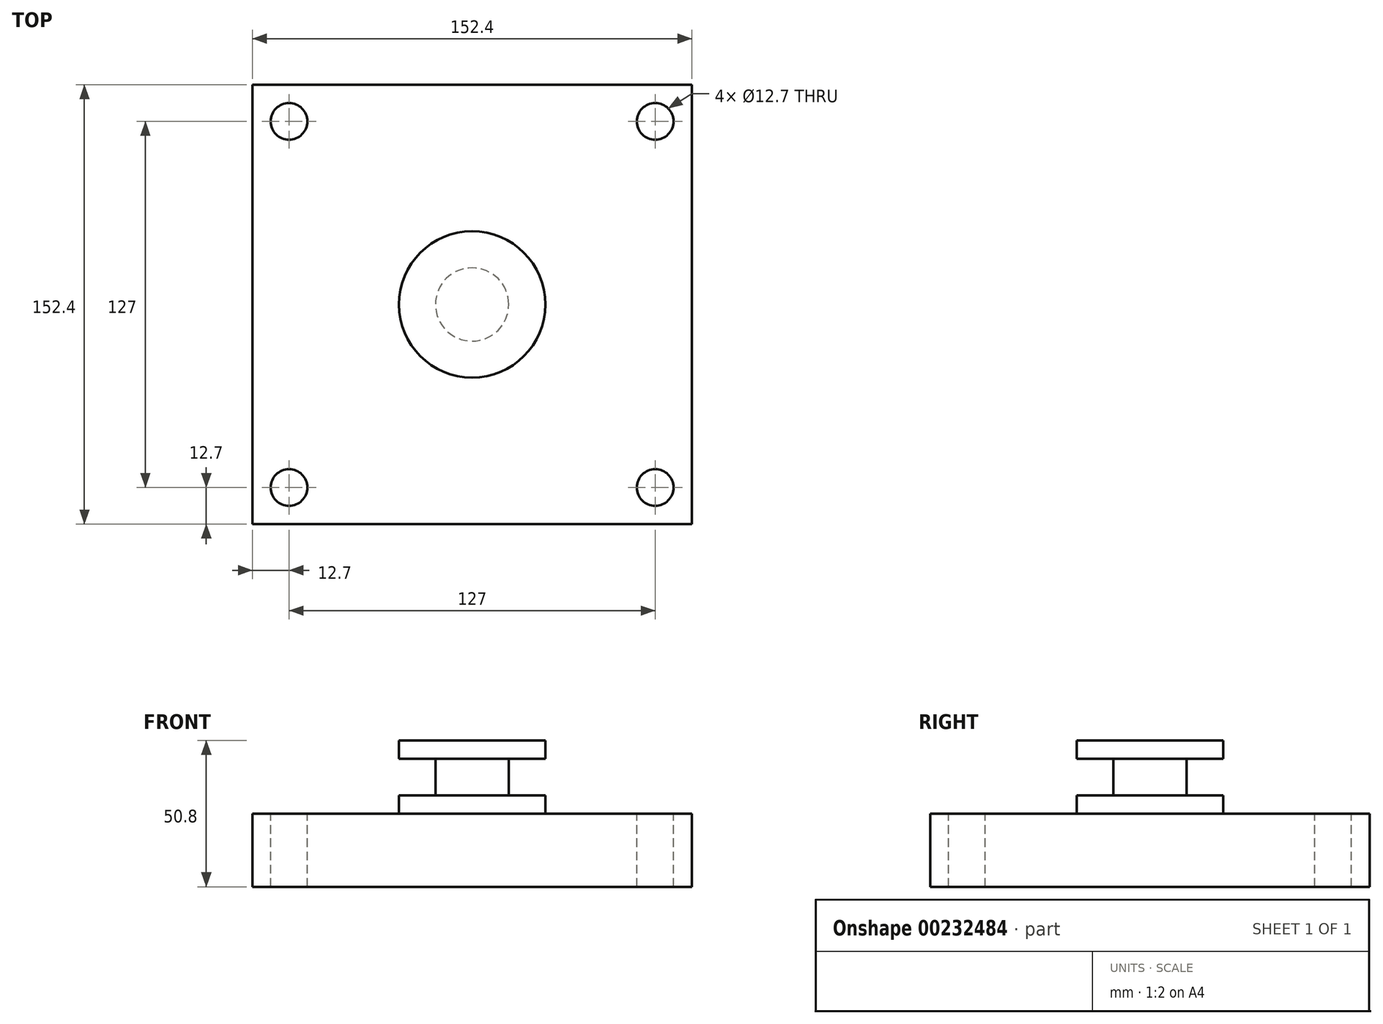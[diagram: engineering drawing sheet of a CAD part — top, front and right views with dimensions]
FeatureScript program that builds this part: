
annotation { "Feature Type Name" : "Feature", "Feature Type Description" : "" }
export const myFeature = defineFeature(function(context is Context, id is Id, definition is map)
    precondition{}
    {
        {
            var Q0;
            Q0=qCreatedBy(makeId("Top.planeOp"),FACE);
            var sketch = newSketch(context, id + "F0", { "sketchPlane" : qUnion([Q0])});
            skLineSegment(sketch, "E0.bottom", {"start": v(76.2, -76.2) * mm, "end": v(-76.2, -76.2) * mm});
            skLineSegment(sketch, "E0.top", {"start": v(76.2, 76.2) * mm, "end": v(-76.2, 76.2) * mm});
            skLineSegment(sketch, "E0.left", {"start": v(76.2, -76.2) * mm, "end": v(76.2, 76.2) * mm});
            skLineSegment(sketch, "E0.right", {"start": v(-76.2, -76.2) * mm, "end": v(-76.2, 76.2) * mm});
            skPoint(sketch, "E0.middle", {"position": v(0, 0) * mm});
            skSolve(sketch);
        }
        {
            var Q0;
            Q0=makeQuery(id+"F0.imprint","IMPRINT",FACE,{"disambiguationData":[TD([[makeQuery(id+"F0.imprint","IMPRINT",EDGE,{"derivedFrom":sQuery(id+"F0.wireOp",EDGE,"E0.bottom")}),-1.0]])]});
            extrude(context, id + "F1", {"entities" : qUnion([Q0]), "depth" : 25.4 * mm});
        }
        {
            var Q0;
            Q0=makeQuery(id+"F1.opExtrude","CAP_FACE",FACE,{"disambiguationData":[OSD([sQuery(id+"F0.wireOp",EDGE,"E0.bottom"),sQuery(id+"F0.wireOp",EDGE,"E0.top"),sQuery(id+"F0.wireOp",EDGE,"E0.left"),sQuery(id+"F0.wireOp",EDGE,"E0.right")])],"isStart":false});
            var sketch = newSketch(context, id + "F2", { "sketchPlane" : qUnion([Q0])});
            skCircle(sketch, "E1", {"center": v(-63.5, 63.5) * mm, "radius": 6.35 * mm});
            skCircle(sketch, "E2", {"center": v(63.5, 63.5) * mm, "radius": 6.35 * mm});
            skCircle(sketch, "E3", {"center": v(63.5, -63.5) * mm, "radius": 6.35 * mm});
            skCircle(sketch, "E4", {"center": v(-63.5, -63.5) * mm, "radius": 6.35 * mm});
            skSolve(sketch);
        }
        {
            var Q0;
            Q0=makeQuery(id+"F2.imprint","IMPRINT",FACE,{"disambiguationData":[TD([[makeQuery(id+"F2.imprint","IMPRINT",EDGE,{"derivedFrom":sQuery(id+"F2.wireOp",EDGE,"E1")}),1.0]])]});
            var Q1;
            Q1=makeQuery(id+"F2.imprint","IMPRINT",FACE,{"disambiguationData":[TD([[makeQuery(id+"F2.imprint","IMPRINT",EDGE,{"derivedFrom":sQuery(id+"F2.wireOp",EDGE,"E2")}),1.0]])]});
            var Q2;
            Q2=makeQuery(id+"F2.imprint","IMPRINT",FACE,{"disambiguationData":[TD([[makeQuery(id+"F2.imprint","IMPRINT",EDGE,{"derivedFrom":sQuery(id+"F2.wireOp",EDGE,"E3")}),1.0]])]});
            var Q3;
            Q3=makeQuery(id+"F2.imprint","IMPRINT",FACE,{"disambiguationData":[TD([[makeQuery(id+"F2.imprint","IMPRINT",EDGE,{"derivedFrom":sQuery(id+"F2.wireOp",EDGE,"E4")}),1.0]])]});
            extrude(context, id + "F3", {"entities" : qUnion([Q0, Q1, Q2, Q3]), "operationType" : NewBodyOperationType.REMOVE, "endBound" : BoundingType.THROUGH_ALL, "oppositeDirection" : true, "depth" : 25.4 * mm});
        }
        {
            var Q0;
            Q0=qCreatedBy(makeId("Front.planeOp"),FACE);
            var sketch = newSketch(context, id + "F4", { "sketchPlane" : qUnion([Q0])});
            skLineSegment(sketch, "E5.bottom", {"start": v(0, 25.4) * mm, "end": v(-25.4, 25.4) * mm});
            skLineSegment(sketch, "E5.top", {"start": v(0, 50.8) * mm, "end": v(-25.4, 50.8) * mm});
            skLineSegment(sketch, "E5.left", {"start": v(0, 25.4) * mm, "end": v(0, 50.8) * mm});
            skLineSegment(sketch, "E5.right", {"start": v(-25.4, 25.4) * mm, "end": v(-25.4, 50.8) * mm});
            skSolve(sketch);
        }
        {
            var Q0;
            Q0=makeQuery(id+"F4.imprint","IMPRINT",FACE,{"disambiguationData":[TD([[makeQuery(id+"F4.imprint","IMPRINT",EDGE,{"derivedFrom":sQuery(id+"F4.wireOp",EDGE,"E5.bottom")}),-1.0]])]});
            var Q1;
            Q1=sQuery(id+"F4.wireOp",EDGE,"E5.left");
            revolve(context, id + "F5", {"operationType" : NewBodyOperationType.ADD, "entities" : qUnion([Q0]), "axis" : qUnion([Q1]), "revolveType" : RevolveType.FULL});
        }
        {
            var Q0;
            Q0=qCreatedBy(makeId("Front.planeOp"),FACE);
            var sketch = newSketch(context, id + "F6", { "sketchPlane" : qUnion([Q0])});
            skLineSegment(sketch, "E6.bottom", {"start": v(-12.7, 31.75) * mm, "end": v(-38.1, 31.75) * mm});
            skLineSegment(sketch, "E6.top", {"start": v(-12.7, 44.45) * mm, "end": v(-38.1, 44.45) * mm});
            skLineSegment(sketch, "E6.left", {"start": v(-12.7, 31.75) * mm, "end": v(-12.7, 44.45) * mm});
            skLineSegment(sketch, "E6.right", {"start": v(-38.1, 31.75) * mm, "end": v(-38.1, 44.45) * mm});
            skSolve(sketch);
        }
        {
            var Q0;
            Q0=makeQuery(id+"F6.imprint","IMPRINT",FACE,{"disambiguationData":[TD([[makeQuery(id+"F6.imprint","IMPRINT",EDGE,{"derivedFrom":sQuery(id+"F6.wireOp",EDGE,"E6.bottom")}),-1.0]])]});
            var Q1;
            Q1=makeQuery(id+"F5.opRevolve","SWEPT_FACE",FACE,{"disambiguationData":[OSD([sQuery(id+"F4.wireOp",EDGE,"E5.right")])]});
            revolve(context, id + "F7", {"operationType" : NewBodyOperationType.REMOVE, "entities" : qUnion([Q0]), "axis" : qUnion([Q1]), "revolveType" : RevolveType.FULL, "oppositeDirection" : true});
        }
    });
